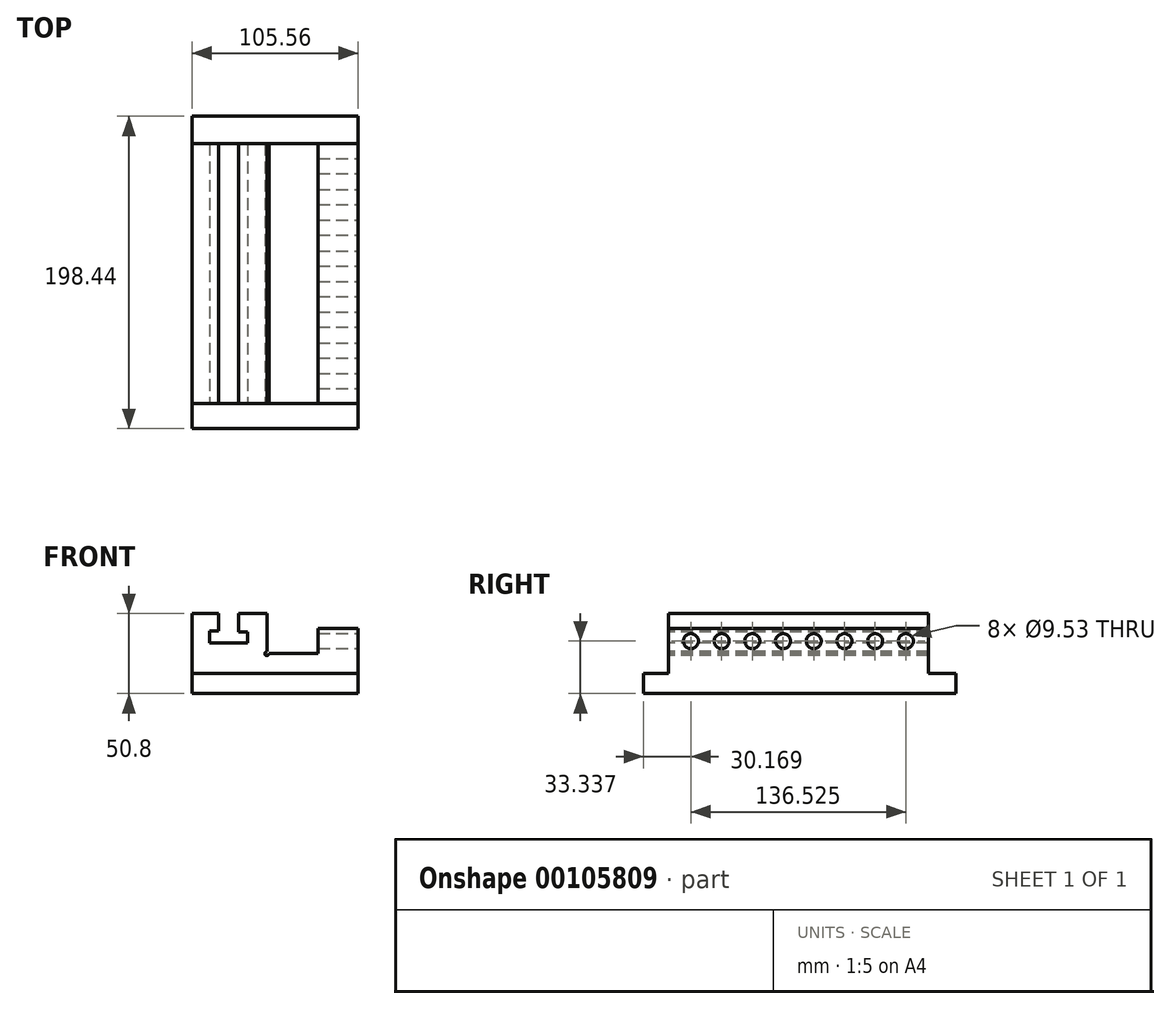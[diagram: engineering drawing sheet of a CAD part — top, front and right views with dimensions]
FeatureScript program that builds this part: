
annotation { "Feature Type Name" : "Feature", "Feature Type Description" : "" }
export const myFeature = defineFeature(function(context is Context, id is Id, definition is map)
    precondition{}
    {
        {
            var Q0;
            Q0=qCreatedBy(makeId("Front.planeOp"),FACE);
            var sketch = newSketch(context, id + "F0", { "sketchPlane" : qUnion([Q0])});
            skLineSegment(sketch, "E0.bottom", {"start": v(0, 0) * mm, "end": v(105.56, 0) * mm});
            skLineSegment(sketch, "E0.top", {"start": v(0, 50.8) * mm, "end": v(105.56, 50.8) * mm});
            skLineSegment(sketch, "E0.left", {"start": v(0, 0) * mm, "end": v(0, 50.8) * mm});
            skLineSegment(sketch, "E0.right", {"start": v(105.56, 0) * mm, "end": v(105.56, 50.8) * mm});
            skSolve(sketch);
        }
        {
            var Q0;
            Q0 = qSketchRegion(id + "F0", true);
            extrude(context, id + "F1", {"entities" : qUnion([Q0]), "oppositeDirection" : true, "depth" : 198.44 * mm});
        }
        {
            var Q0;
            Q0=makeQuery(id+"F1.opExtrude","CAP_FACE",FACE,{"disambiguationData":[OSD([sQuery(id+"F0.wireOp",EDGE,"E0.bottom"),sQuery(id+"F0.wireOp",EDGE,"E0.top"),sQuery(id+"F0.wireOp",EDGE,"E0.left"),sQuery(id+"F0.wireOp",EDGE,"E0.right")])],"isStart":true});
            var sketch = newSketch(context, id + "F2", { "sketchPlane" : qUnion([Q0])});
            skLineSegment(sketch, "E1.bottom", {"start": v(0, 50.8) * mm, "end": v(105.56, 50.8) * mm});
            skLineSegment(sketch, "E1.top", {"start": v(0, 12.7) * mm, "end": v(105.56, 12.7) * mm});
            skLineSegment(sketch, "E1.left", {"start": v(0, 50.8) * mm, "end": v(0, 12.7) * mm});
            skLineSegment(sketch, "E1.right", {"start": v(105.56, 50.8) * mm, "end": v(105.56, 12.7) * mm});
            skSolve(sketch);
        }
        {
            var Q0;
            Q0 = qSketchRegion(id + "F2", true);
            extrude(context, id + "F3", {"entities" : qUnion([Q0]), "operationType" : NewBodyOperationType.REMOVE, "oppositeDirection" : true, "depth" : 15.88 * mm});
        }
        {
            var Q0;
            Q0=makeQuery(id+"F3.boolean.opBoolean","COPY",FACE,{"derivedFrom":makeQuery(id+"F3.opExtrude","CAP_FACE",FACE,{"disambiguationData":[OSD([sQuery(id+"F2.wireOp",EDGE,"E1.bottom"),sQuery(id+"F2.wireOp",EDGE,"E1.top"),sQuery(id+"F2.wireOp",EDGE,"E1.left"),sQuery(id+"F2.wireOp",EDGE,"E1.right")])],"isStart":false})});
            var sketch = newSketch(context, id + "F4", { "sketchPlane" : qUnion([Q0])});
            skLineSegment(sketch, "E2", {"start": v(16.93, 50.8) * mm, "end": v(16.93, 39.69) * mm});
            skLineSegment(sketch, "E3", {"start": v(16.93, 39.69) * mm, "end": v(11.24, 39.69) * mm});
            skLineSegment(sketch, "E4", {"start": v(11.24, 39.69) * mm, "end": v(11.24, 32.07) * mm});
            skLineSegment(sketch, "E5", {"start": v(11.24, 32.07) * mm, "end": v(35.45, 32.07) * mm});
            skLineSegment(sketch, "E6", {"start": v(35.45, 32.07) * mm, "end": v(35.45, 39.3) * mm});
            skLineSegment(sketch, "E7", {"start": v(35.45, 39.3) * mm, "end": v(29.77, 39.3) * mm});
            skLineSegment(sketch, "E8", {"start": v(29.77, 39.3) * mm, "end": v(29.77, 50.8) * mm});
            skLineSegment(sketch, "E9", {"start": v(29.77, 50.8) * mm, "end": v(16.93, 50.8) * mm});
            skLineSegment(sketch, "E10", {"start": v(80.16, 25.4) * mm, "end": v(47.62, 25.4) * mm});
            skLineSegment(sketch, "E11", {"start": v(47.62, 25.4) * mm, "end": v(47.62, 50.8) * mm});
            skLineSegment(sketch, "E12", {"start": v(47.62, 50.8) * mm, "end": v(105.56, 50.8) * mm});
            skLineSegment(sketch, "E13", {"start": v(80.16, 25.4) * mm, "end": v(80.16, 41.28) * mm});
            skLineSegment(sketch, "E14", {"start": v(80.16, 41.28) * mm, "end": v(105.56, 41.28) * mm});
            skSolve(sketch);
        }
        {
            var Q0;
            Q0 = qSketchRegion(id + "F4", true);
            var Q1;
            Q1=makeQuery(id+"F4.imprint","IMPRINT",FACE,{"disambiguationData":[TD([[makeQuery(id+"F4.imprint","IMPRINT",EDGE,{"derivedFrom":sQuery(id+"F4.wireOp",EDGE,"E10")}),-1.0]])]});
            extrude(context, id + "F5", {"entities" : qUnion([Q0, Q1]), "operationType" : NewBodyOperationType.REMOVE, "endBound" : BoundingType.THROUGH_ALL, "oppositeDirection" : true, "depth" : 25.4 * mm});
        }
        {
            var Q0;
            Q0=makeQuery(id+"F1.opExtrude","CAP_FACE",FACE,{"disambiguationData":[OSD([sQuery(id+"F0.wireOp",EDGE,"E0.bottom"),sQuery(id+"F0.wireOp",EDGE,"E0.top"),sQuery(id+"F0.wireOp",EDGE,"E0.left"),sQuery(id+"F0.wireOp",EDGE,"E0.right")])],"isStart":false});
            var sketch = newSketch(context, id + "F6", { "sketchPlane" : qUnion([Q0])});
            skLineSegment(sketch, "E15.bottom", {"start": v(0, 50.8) * mm, "end": v(-105.56, 50.8) * mm});
            skLineSegment(sketch, "E15.top", {"start": v(0, 12.7) * mm, "end": v(-105.56, 12.7) * mm});
            skLineSegment(sketch, "E15.left", {"start": v(0, 50.8) * mm, "end": v(0, 12.7) * mm});
            skLineSegment(sketch, "E15.right", {"start": v(-105.56, 50.8) * mm, "end": v(-105.56, 12.7) * mm});
            skSolve(sketch);
        }
        {
            var Q0;
            Q0 = qSketchRegion(id + "F6", true);
            extrude(context, id + "F7", {"entities" : qUnion([Q0]), "operationType" : NewBodyOperationType.REMOVE, "oppositeDirection" : true, "depth" : 17.45 * mm});
        }
        {
            var Q0;
            Q0=makeQuery(id+"F1.opExtrude","SWEPT_FACE",FACE,{"disambiguationData":[OSD([sQuery(id+"F0.wireOp",EDGE,"E0.right")])]});
            var sketch = newSketch(context, id + "F8", { "sketchPlane" : qUnion([Q0])});
            skCircle(sketch, "E16", {"center": v(30.17, 33.34) * mm, "radius": 4.76 * mm});
            skCircle(sketch, "E17", {"center": v(49.67, 33.34) * mm, "radius": 4.76 * mm});
            skCircle(sketch, "E18", {"center": v(69.18, 33.34) * mm, "radius": 4.76 * mm});
            skCircle(sketch, "E19", {"center": v(88.68, 33.34) * mm, "radius": 4.76 * mm});
            skCircle(sketch, "E20", {"center": v(108.18, 33.34) * mm, "radius": 4.76 * mm});
            skCircle(sketch, "E21", {"center": v(127.69, 33.34) * mm, "radius": 4.76 * mm});
            skCircle(sketch, "E22", {"center": v(147.2, 33.34) * mm, "radius": 4.76 * mm});
            skCircle(sketch, "E23", {"center": v(166.7, 33.34) * mm, "radius": 4.76 * mm});
            skLineSegment(sketch, "E24", {"start": v(30.17, 33.34) * mm, "end": v(15.88, 33.34) * mm});
            skLineSegment(sketch, "E25", {"start": v(166.7, 33.34) * mm, "end": v(180.99, 33.34) * mm});
            skLineSegment(sketch, "E26", {"start": v(30.17, 33.34) * mm, "end": v(49.67, 33.34) * mm});
            skLineSegment(sketch, "E27", {"start": v(49.67, 33.34) * mm, "end": v(69.18, 33.34) * mm});
            skLineSegment(sketch, "E28", {"start": v(69.18, 33.34) * mm, "end": v(88.68, 33.34) * mm});
            skLineSegment(sketch, "E29", {"start": v(88.68, 33.34) * mm, "end": v(108.18, 33.34) * mm});
            skLineSegment(sketch, "E30", {"start": v(108.18, 33.34) * mm, "end": v(127.69, 33.34) * mm});
            skLineSegment(sketch, "E31", {"start": v(127.69, 33.34) * mm, "end": v(147.2, 33.34) * mm});
            skLineSegment(sketch, "E32", {"start": v(147.2, 33.34) * mm, "end": v(166.7, 33.34) * mm});
            skSolve(sketch);
        }
        {
            var Q0;
            Q0 = qSketchRegion(id + "F8", true);
            extrude(context, id + "F9", {"entities" : qUnion([Q0]), "operationType" : NewBodyOperationType.REMOVE, "endBound" : BoundingType.UP_TO_NEXT, "oppositeDirection" : true, "depth" : 25.4 * mm});
        }
        {
            var Q0;
            Q0=makeQuery(id+"F3.boolean.opBoolean","COPY",FACE,{"derivedFrom":makeQuery(id+"F3.opExtrude","CAP_FACE",FACE,{"disambiguationData":[OSD([sQuery(id+"F2.wireOp",EDGE,"E1.bottom"),sQuery(id+"F2.wireOp",EDGE,"E1.top"),sQuery(id+"F2.wireOp",EDGE,"E1.left"),sQuery(id+"F2.wireOp",EDGE,"E1.right")])],"isStart":false})});
            var sketch = newSketch(context, id + "F10", { "sketchPlane" : qUnion([Q0])});
            skCircle(sketch, "E33", {"center": v(47.62, 25.4) * mm, "radius": 1.27 * mm});
            skSolve(sketch);
        }
        {
            var Q0;
            Q0 = qSketchRegion(id + "F10", true);
            extrude(context, id + "F11", {"entities" : qUnion([Q0]), "operationType" : NewBodyOperationType.REMOVE, "endBound" : BoundingType.THROUGH_ALL, "oppositeDirection" : true, "depth" : 25.4 * mm});
        }
    });
